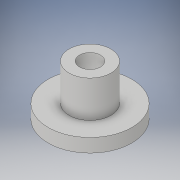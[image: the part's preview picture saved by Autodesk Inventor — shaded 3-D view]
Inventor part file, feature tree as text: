
AUTODESK INVENTOR PART (.ipt)
format: ipt  version: 2018 (Build 220112000, 112)  size: 108,032 bytes
history: native  units: in
note: dims shown in document units (in); Inventor stores cm internally (conversion verified against a paired STEP export)
features: revolve x1, sketch x1
ambient origin geometry x8: Origin, YZ Plane, XZ Plane, XY Plane, X Axis, Y Axis, Z Axis, Center Point
bodies: Solid1 (feature_tree)
feature tree (2):
  revolve  "Revolution1"  [1 undecoded]
  sketch  "Sketch1"  dims[d0=0.0492in d1=0.2362in d2=0.1969in d3=0.0492in d4=90.0deg]
note: 1 required parameter value undecoded (feature->parameter linkage not recoverable at this tier; creation-order binding heuristic only, values carry confidence <= 0.55)
